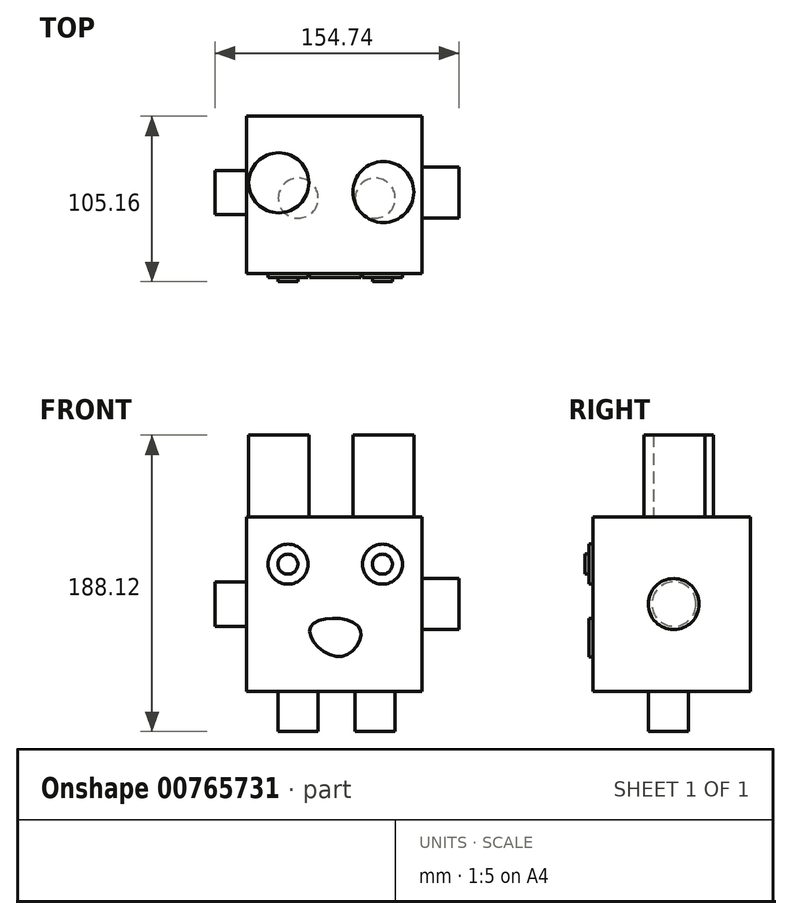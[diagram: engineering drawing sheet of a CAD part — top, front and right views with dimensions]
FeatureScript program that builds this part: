
annotation { "Feature Type Name" : "Feature", "Feature Type Description" : "" }
export const myFeature = defineFeature(function(context is Context, id is Id, definition is map)
    precondition{}
    {
        {
            var Q0;
            Q0=qCreatedBy(makeId("Front.planeOp"),FACE);
            var sketch = newSketch(context, id + "F0", { "sketchPlane" : qUnion([Q0])});
            skLineSegment(sketch, "E0.bottom", {"start": v(55.65, 55.45) * mm, "end": v(-55.65, 55.45) * mm});
            skLineSegment(sketch, "E0.top", {"start": v(55.65, -55.45) * mm, "end": v(-55.65, -55.45) * mm});
            skLineSegment(sketch, "E0.left", {"start": v(55.65, 55.45) * mm, "end": v(55.65, -55.45) * mm});
            skLineSegment(sketch, "E0.right", {"start": v(-55.65, 55.45) * mm, "end": v(-55.65, -55.45) * mm});
            skPoint(sketch, "E0.middle", {"position": v(0, 0) * mm});
            skSolve(sketch);
        }
        {
            var Q0;
            Q0 = qSketchRegion(id + "F0", true);
            extrude(context, id + "F1", {"entities" : qUnion([Q0]), "depth" : 100.08 * mm, "offsetDistance" : 25.4 * mm});
        }
        {
            var Q0;
            Q0=makeQuery(id+"F1.opExtrude","SWEPT_FACE",FACE,{"disambiguationData":[OSD([sQuery(id+"F0.wireOp",EDGE,"E0.bottom")])]});
            var sketch = newSketch(context, id + "F2", { "sketchPlane" : qUnion([Q0])});
            skPoint(sketch, "E1", {"position": v(-35.28, -42.34) * mm});
            skPoint(sketch, "E2", {"position": v(31.14, -48.2) * mm});
            skCircle(sketch, "E3", {"center": v(-35.28, -42.34) * mm, "radius": 19.07 * mm});
            skCircle(sketch, "E4", {"center": v(31.14, -48.2) * mm, "radius": 19.35 * mm});
            skSolve(sketch);
        }
        {
            var Q0;
            Q0 = qSketchRegion(id + "F2", true);
            extrude(context, id + "F3", {"entities" : qUnion([Q0]), "operationType" : NewBodyOperationType.ADD, "depth" : 51.82 * mm, "offsetDistance" : 25.4 * mm});
        }
        {
            var Q0;
            Q0=makeQuery(id+"F1.opExtrude","CAP_FACE",FACE,{"disambiguationData":[OSD([sQuery(id+"F0.wireOp",EDGE,"E0.bottom"),sQuery(id+"F0.wireOp",EDGE,"E0.top"),sQuery(id+"F0.wireOp",EDGE,"E0.left"),sQuery(id+"F0.wireOp",EDGE,"E0.right")])],"isStart":false});
            var sketch = newSketch(context, id + "F4", { "sketchPlane" : qUnion([Q0])});
            skPoint(sketch, "E5", {"position": v(-29.46, 25.34) * mm});
            skCircle(sketch, "E6", {"center": v(-29.46, 25.34) * mm, "radius": 12.7 * mm});
            skPoint(sketch, "E7", {"position": v(30.56, 25.34) * mm});
            skCircle(sketch, "E8", {"center": v(30.56, 25.34) * mm, "radius": 12.7 * mm});
            skCircle(sketch, "E9", {"center": v(-29.46, 25.34) * mm, "radius": 6.35 * mm});
            skCircle(sketch, "E10", {"center": v(30.56, 25.34) * mm, "radius": 6.35 * mm});
            skSolve(sketch);
        }
        {
            var Q0;
            Q0 = qSketchRegion(id + "F4", true);
            extrude(context, id + "F5", {"entities" : qUnion([Q0]), "operationType" : NewBodyOperationType.ADD, "depth" : 2.54 * mm, "offsetDistance" : 25.4 * mm});
        }
        {
            var Q0;
            Q0=makeQuery(id+"F5.boolean.opBoolean","SPLIT",FACE,{"disambiguationData":[TD([makeQuery(id+"F5.opExtrude","SWEPT_FACE",FACE,{"disambiguationData":[OSD([sQuery(id+"F4.wireOp",EDGE,"E9")])]})])],"derivedFrom":makeQuery(id+"F1.opExtrude","CAP_FACE",FACE,{"disambiguationData":[OSD([sQuery(id+"F0.wireOp",EDGE,"E0.bottom"),sQuery(id+"F0.wireOp",EDGE,"E0.top"),sQuery(id+"F0.wireOp",EDGE,"E0.left"),sQuery(id+"F0.wireOp",EDGE,"E0.right")])],"isStart":false})});
            var Q1;
            Q1=makeQuery(id+"F5.boolean.opBoolean","SPLIT",FACE,{"disambiguationData":[TD([makeQuery(id+"F5.opExtrude","SWEPT_FACE",FACE,{"disambiguationData":[OSD([sQuery(id+"F4.wireOp",EDGE,"E10")])]})])],"derivedFrom":makeQuery(id+"F1.opExtrude","CAP_FACE",FACE,{"disambiguationData":[OSD([sQuery(id+"F0.wireOp",EDGE,"E0.bottom"),sQuery(id+"F0.wireOp",EDGE,"E0.top"),sQuery(id+"F0.wireOp",EDGE,"E0.left"),sQuery(id+"F0.wireOp",EDGE,"E0.right")])],"isStart":false})});
            extrude(context, id + "F6", {"entities" : qUnion([Q0, Q1]), "operationType" : NewBodyOperationType.ADD, "depth" : 5.08 * mm, "offsetDistance" : 25.4 * mm});
        }
        {
            var Q0;
            {var subQ0=sQuery(id+"F0.wireOp",EDGE,"E0.left");var subQ1=sQuery(id+"F0.wireOp",EDGE,"E0.top");var subQ2=sQuery(id+"F0.wireOp",EDGE,"E0.right");var subQ3=sQuery(id+"F0.wireOp",EDGE,"E0.bottom");Q0=makeQuery(id+"F5.boolean.opBoolean","SPLIT",FACE,{"disambiguationData":[TD([makeQuery(id+"F1.opExtrude","SWEPT_FACE",FACE,{"disambiguationData":[OSD([subQ3])]})])],"derivedFrom":makeQuery(id+"F1.opExtrude","CAP_FACE",FACE,{"disambiguationData":[OSD([subQ3,subQ1,subQ0,subQ2])],"isStart":false})});}
            var sketch = newSketch(context, id + "F7", { "sketchPlane" : qUnion([Q0])});
            skFitSpline(sketch, "E11", {"points": [v(-15.2, -14.53) * mm, v(15.45, -14.53) * mm, v(3.7, -33.42) * mm, v(-15.2, -14.53) * mm]});
            skSolve(sketch);
        }
        {
            var Q0;
            Q0 = qSketchRegion(id + "F7", true);
            extrude(context, id + "F8", {"entities" : qUnion([Q0]), "operationType" : NewBodyOperationType.ADD, "depth" : 2.54 * mm, "offsetDistance" : 25.4 * mm});
        }
        {
            var Q0;
            {var subQ0=sQuery(id+"F0.wireOp",EDGE,"E0.left");var subQ1=sQuery(id+"F0.wireOp",EDGE,"E0.top");var subQ2=sQuery(id+"F0.wireOp",EDGE,"E0.right");var subQ3=sQuery(id+"F0.wireOp",EDGE,"E0.bottom");Q0=makeQuery(id+"F5.boolean.opBoolean","SPLIT",FACE,{"disambiguationData":[TD([makeQuery(id+"F1.opExtrude","SWEPT_FACE",FACE,{"disambiguationData":[OSD([subQ3])]})])],"derivedFrom":makeQuery(id+"F1.opExtrude","CAP_FACE",FACE,{"disambiguationData":[OSD([subQ3,subQ1,subQ0,subQ2])],"isStart":false})});}
            var sketch = newSketch(context, id + "F9", { "sketchPlane" : qUnion([Q0])});
            skSolve(sketch);
        }
        {
            var Q0;
            Q0=makeQuery(id+"F1.opExtrude","SWEPT_FACE",FACE,{"disambiguationData":[OSD([sQuery(id+"F0.wireOp",EDGE,"E0.right")])]});
            var sketch = newSketch(context, id + "F10", { "sketchPlane" : qUnion([Q0])});
            skPoint(sketch, "E12", {"position": v(48.53, 0) * mm});
            skCircle(sketch, "E13", {"center": v(48.53, 0) * mm, "radius": 14.05 * mm});
            skSolve(sketch);
        }
        {
            var Q0;
            Q0 = qSketchRegion(id + "F10", true);
            extrude(context, id + "F11", {"entities" : qUnion([Q0]), "operationType" : NewBodyOperationType.ADD, "depth" : 20.07 * mm, "offsetDistance" : 25.4 * mm});
        }
        {
            var Q0;
            Q0=makeQuery(id+"F1.opExtrude","SWEPT_FACE",FACE,{"disambiguationData":[OSD([sQuery(id+"F0.wireOp",EDGE,"E0.left")])]});
            var sketch = newSketch(context, id + "F12", { "sketchPlane" : qUnion([Q0])});
            skPoint(sketch, "E14", {"position": v(-48.64, 0) * mm});
            skCircle(sketch, "E15", {"center": v(-48.64, 0) * mm, "radius": 16.17 * mm});
            skSolve(sketch);
        }
        {
            var Q0;
            Q0 = qSketchRegion(id + "F12", true);
            extrude(context, id + "F13", {"entities" : qUnion([Q0]), "operationType" : NewBodyOperationType.ADD, "depth" : 23.37 * mm, "offsetDistance" : 25.4 * mm});
        }
        {
            var Q0;
            Q0=makeQuery(id+"F1.opExtrude","SWEPT_FACE",FACE,{"disambiguationData":[OSD([sQuery(id+"F0.wireOp",EDGE,"E0.top")])]});
            var sketch = newSketch(context, id + "F14", { "sketchPlane" : qUnion([Q0])});
            skPoint(sketch, "E16", {"position": v(-22.94, 52.12) * mm});
            skPoint(sketch, "E17", {"position": v(25.96, 52.12) * mm});
            skCircle(sketch, "E18", {"center": v(-22.94, 52.12) * mm, "radius": 12.7 * mm});
            skCircle(sketch, "E19", {"center": v(25.96, 52.12) * mm, "radius": 12.7 * mm});
            skSolve(sketch);
        }
        {
            var Q0;
            Q0 = qSketchRegion(id + "F14", true);
            extrude(context, id + "F15", {"entities" : qUnion([Q0]), "operationType" : NewBodyOperationType.ADD, "depth" : 25.4 * mm, "offsetDistance" : 25.4 * mm});
        }
    });
